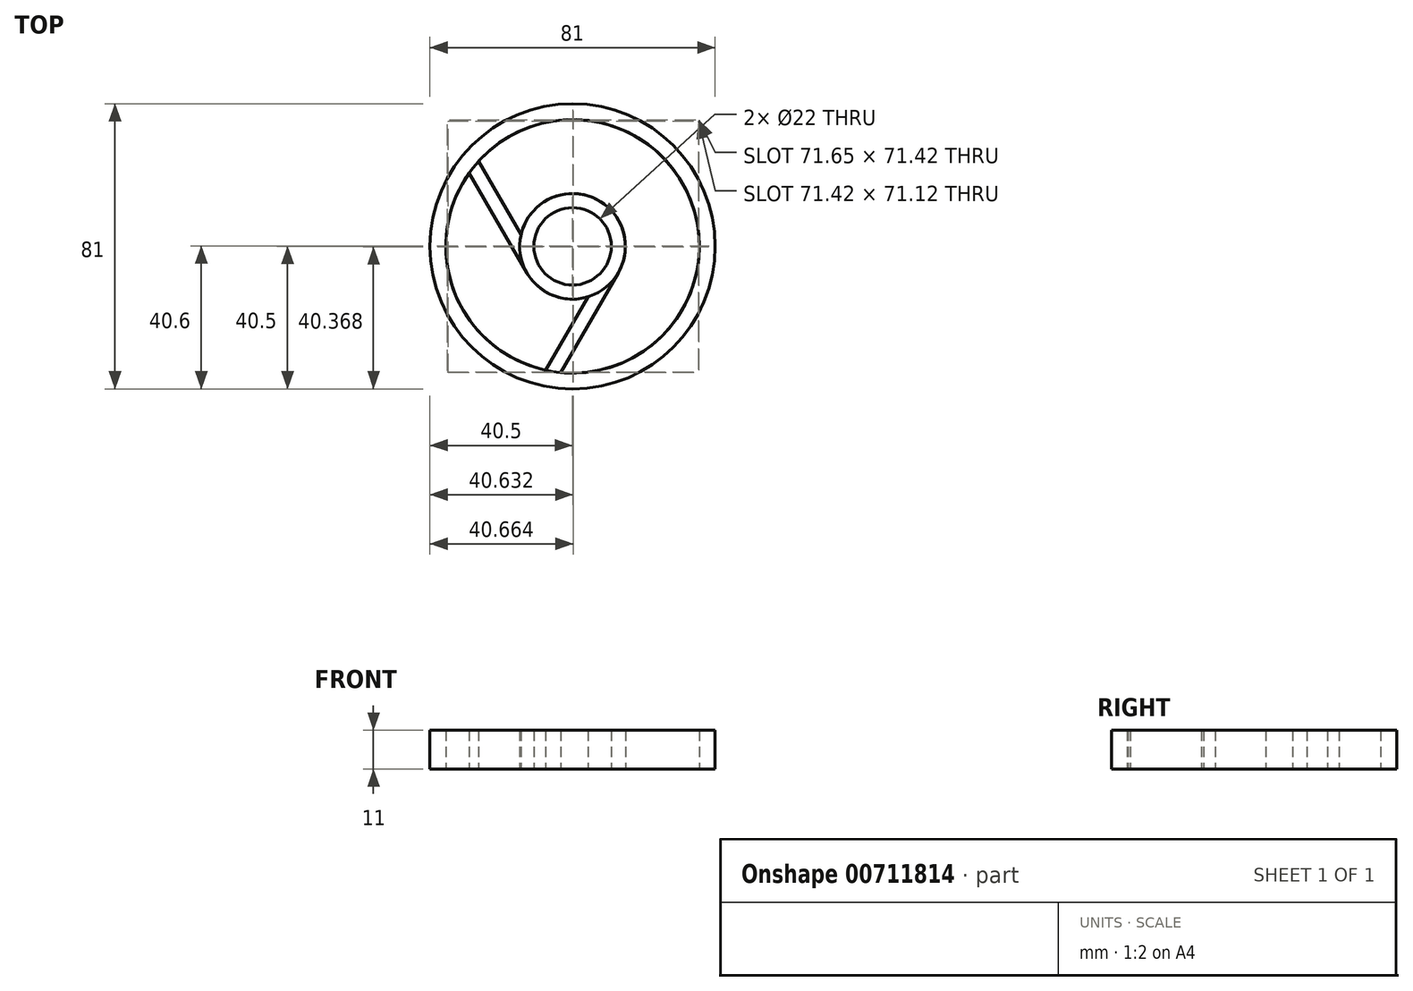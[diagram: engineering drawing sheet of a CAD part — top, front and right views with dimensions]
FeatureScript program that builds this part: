
annotation { "Feature Type Name" : "Feature", "Feature Type Description" : "" }
export const myFeature = defineFeature(function(context is Context, id is Id, definition is map)
    precondition{}
    {
        {
            var Q0;
            Q0=qCreatedBy(makeId("Top.planeOp"),FACE);
            var sketch = newSketch(context, id + "F0", { "sketchPlane" : qUnion([Q0])});
            skCircle(sketch, "E0", {"center": v(0, 0) * mm, "radius": 40.5 * mm});
            skCircle(sketch, "E1", {"center": v(0, 0) * mm, "radius": 36 * mm});
            skCircle(sketch, "E2", {"center": v(0, 0) * mm, "radius": 11 * mm});
            skCircle(sketch, "E3", {"center": v(0, 0) * mm, "radius": 15 * mm});
            skLineSegment(sketch, "E4", {"start": v(0, 15) * mm, "end": v(37.62, 15) * mm});
            skLineSegment(sketch, "E5", {"start": v(0, 11) * mm, "end": v(38.98, 11) * mm});
            skSolve(sketch);
        }
        {
            var Q0;
            {var subQ0=sQuery(id+"F0.wireOp",EDGE,"E4");var subQ1=sQuery(id+"F0.wireOp",EDGE,"E0");var subQ2=makeQuery(id+"F0.imprint","INTERSECT",VERTEX,{"derivedFrom":[subQ1,subQ0]});Q0=makeQuery(id+"F0.imprint","IMPRINT",FACE,{"disambiguationData":[TD([[makeQuery(id+"F0.imprint","IMPRINT",EDGE,{"disambiguationData":[TD([[subQ2,-1.0]])],"derivedFrom":subQ1}),1.0]])]});}
            var Q1;
            Q1=makeQuery(id+"F0.imprint","IMPRINT",FACE,{"disambiguationData":[TD([[makeQuery(id+"F0.imprint","IMPRINT",EDGE,{"derivedFrom":sQuery(id+"F0.wireOp",EDGE,"E2")}),-1.0]])]});
            var Q2;
            {var subQ0=sQuery(id+"F0.wireOp",EDGE,"E4");var subQ1=sQuery(id+"F0.wireOp",EDGE,"E1");var subQ2=makeQuery(id+"F0.imprint","INTERSECT",VERTEX,{"derivedFrom":[subQ1,subQ0]});Q2=makeQuery(id+"F0.imprint","IMPRINT",FACE,{"disambiguationData":[TD([[makeQuery(id+"F0.imprint","IMPRINT",EDGE,{"disambiguationData":[TD([[subQ2,1.0]])],"derivedFrom":subQ1}),1.0]])]});}
            var Q3;
            {var subQ0=sQuery(id+"F0.wireOp",EDGE,"E4");var subQ1=sQuery(id+"F0.wireOp",EDGE,"E0");var subQ2=makeQuery(id+"F0.imprint","INTERSECT",VERTEX,{"derivedFrom":[subQ1,subQ0]});Q3=makeQuery(id+"F0.imprint","IMPRINT",FACE,{"disambiguationData":[TD([[makeQuery(id+"F0.imprint","IMPRINT",EDGE,{"disambiguationData":[TD([[subQ2,1.0]])],"derivedFrom":subQ1}),1.0]])]});}
            extrude(context, id + "F1", {"entities" : qUnion([Q0, Q1, Q2, Q3]), "endBound" : BoundingType.SYMMETRIC, "depth" : 11 * mm, "offsetDistance" : 25 * mm});
        }
        {
            var Q0;
            Q0=makeQuery(id+"F1.opExtrude","SWEPT_BODY",BODY,{"disambiguationData":[OSD([sQuery(id+"F0.wireOp",EDGE,"E0"),sQuery(id+"F0.wireOp",EDGE,"E1"),sQuery(id+"F0.wireOp",EDGE,"E2"),sQuery(id+"F0.wireOp",EDGE,"E3"),sQuery(id+"F0.wireOp",EDGE,"E4"),sQuery(id+"F0.wireOp",EDGE,"E5")])]});
            var Q1;
            Q1=makeQuery(id+"F1.opExtrude","CAP_EDGE",EDGE,{"disambiguationData":[OSD([sQuery(id+"F0.wireOp",EDGE,"E2")])],"isStart":false});
            transform(context, id + "F2", {"entities" : qUnion([Q0]), "transformType" : TransformType.ROTATION, "transformAxis" : qUnion([Q1]), "angle" : 120 * degree, "makeCopy" : true});
        }
        {
            var Q0;
            Q0=makeQuery(id+"F1.opExtrude","SWEPT_BODY",BODY,{"disambiguationData":[OSD([sQuery(id+"F0.wireOp",EDGE,"E0"),sQuery(id+"F0.wireOp",EDGE,"E1"),sQuery(id+"F0.wireOp",EDGE,"E2"),sQuery(id+"F0.wireOp",EDGE,"E3"),sQuery(id+"F0.wireOp",EDGE,"E4"),sQuery(id+"F0.wireOp",EDGE,"E5")])]});
            var Q1;
            Q1=makeQuery(id+"F1.opExtrude","CAP_EDGE",EDGE,{"disambiguationData":[OSD([sQuery(id+"F0.wireOp",EDGE,"E2")])],"isStart":false});
            transform(context, id + "F3", {"entities" : qUnion([Q0]), "transformType" : TransformType.ROTATION, "transformAxis" : qUnion([Q1]), "angle" : 240 * degree, "makeCopy" : true});
        }
        {
            var Q0;
            Q0=qCreatedBy(makeId("Top.planeOp"),FACE);
            var sketch = newSketch(context, id + "F4", { "sketchPlane" : qUnion([Q0])});
            skLineSegment(sketch, "E6", {"start": v(-5.67, 15.8) * mm, "end": v(5.3, 15.8) * mm});
            skLineSegment(sketch, "E7", {"start": v(5.3, 15.8) * mm, "end": v(10.78, 25.3) * mm});
            skLineSegment(sketch, "E8", {"start": v(10.78, 25.3) * mm, "end": v(5.3, 34.8) * mm});
            skLineSegment(sketch, "E9", {"start": v(5.3, 34.8) * mm, "end": v(-5.67, 34.8) * mm});
            skLineSegment(sketch, "E10", {"start": v(-5.67, 34.8) * mm, "end": v(-11.16, 25.3) * mm});
            skLineSegment(sketch, "E11", {"start": v(-11.16, 25.3) * mm, "end": v(-5.67, 15.8) * mm});
            skLineSegment(sketch, "E12", {"start": v(5.3, 34.8) * mm, "end": v(5.3, 15.8) * mm, "construction": true});
            skLineSegment(sketch, "E13", {"start": v(-5.67, 34.8) * mm, "end": v(10.78, 25.3) * mm, "construction": true});
            skLineSegment(sketch, "E14", {"start": v(-11.16, 25.3) * mm, "end": v(5.3, 34.8) * mm, "construction": true});
            skLineSegment(sketch, "E15", {"start": v(0, 0) * mm, "end": v(0, 15.8) * mm, "construction": true});
            skSolve(sketch);
        }
        {
            var Q0;
            Q0=qSketchRegion(id+"F4",true);
            extrude(context, id + "F5", {"entities" : qUnion([Q0]), "operationType" : NewBodyOperationType.REMOVE, "endBound" : BoundingType.SYMMETRIC, "depth" : 11 * mm, "offsetDistance" : 25 * mm});
        }
        {
            var Q0;
            Q0=qCreatedBy(makeId("Top.planeOp"),FACE);
            var sketch = newSketch(context, id + "F6", { "sketchPlane" : qUnion([Q0])});
            skCircle(sketch, "E16", {"center": v(0, 0) * mm, "radius": 36 * mm});
            skCircle(sketch, "E17", {"center": v(0, 0) * mm, "radius": 15 * mm});
            skSolve(sketch);
        }
        {
            var Q0;
            Q0 = qSketchRegion(id + "F6", true);
            extrude(context, id + "F7", {"entities" : qUnion([Q0]), "endBound" : BoundingType.SYMMETRIC, "depth" : 11 * mm, "offsetDistance" : 25 * mm});
        }
        {
            var Q0;
            Q0=makeQuery(id+"F1.opExtrude","SWEPT_BODY",BODY,{"disambiguationData":[OSD([sQuery(id+"F0.wireOp",EDGE,"E0"),sQuery(id+"F0.wireOp",EDGE,"E1"),sQuery(id+"F0.wireOp",EDGE,"E2"),sQuery(id+"F0.wireOp",EDGE,"E3"),sQuery(id+"F0.wireOp",EDGE,"E4"),sQuery(id+"F0.wireOp",EDGE,"E5")])]});
            var Q1;
            Q1=makeQuery(id+"F7.opExtrude","SWEPT_BODY",BODY,{"disambiguationData":[OSD([sQuery(id+"F6.wireOp",EDGE,"E16"),sQuery(id+"F6.wireOp",EDGE,"E17")])]});
            booleanBodies(context, id + "F8", {"operationType" : BooleanOperationType.SUBTRACTION, "tools" : qUnion([Q0]), "targets" : qUnion([Q1])});
        }
        {
            var Q0;
            Q0=makeQuery(id+"F8.opBoolean","SPLIT",BODY,{"disambiguationData":[OD(1.0)],"derivedFrom":makeQuery(id+"F7.opExtrude","SWEPT_BODY",BODY,{"disambiguationData":[OSD([sQuery(id+"F6.wireOp",EDGE,"E16"),sQuery(id+"F6.wireOp",EDGE,"E17")])]})});
            var Q1;
            Q1=makeQuery(id+"F8.opBoolean","SPLIT",BODY,{"disambiguationData":[OD(2.0)],"derivedFrom":makeQuery(id+"F7.opExtrude","SWEPT_BODY",BODY,{"disambiguationData":[OSD([sQuery(id+"F6.wireOp",EDGE,"E16"),sQuery(id+"F6.wireOp",EDGE,"E17")])]})});
            deleteBodies(context, id + "F9", {"entities" : qUnion([Q0, Q1])});
        }
        {
            var Q0;
            Q0=qCreatedBy(makeId("Top.planeOp"),FACE);
            var sketch = newSketch(context, id + "F10", { "sketchPlane" : qUnion([Q0])});
            skCircle(sketch, "E18.cCircle", {"center": v(0, 25.3) * mm, "radius": 9.5 * mm, "construction": true});
            skLineSegment(sketch, "E18.0", {"start": v(10.97, 25.3) * mm, "end": v(5.48, 15.8) * mm});
            skLineSegment(sketch, "E18.1", {"start": v(5.48, 15.8) * mm, "end": v(-5.48, 15.8) * mm});
            skLineSegment(sketch, "E18.2", {"start": v(-5.48, 15.8) * mm, "end": v(-10.97, 25.3) * mm});
            skLineSegment(sketch, "E18.3", {"start": v(-10.97, 25.3) * mm, "end": v(-5.48, 34.8) * mm});
            skLineSegment(sketch, "E18.4", {"start": v(-5.48, 34.8) * mm, "end": v(5.48, 34.8) * mm});
            skLineSegment(sketch, "E18.5", {"start": v(5.48, 34.8) * mm, "end": v(10.97, 25.3) * mm});
            skPoint(sketch, "E18.0.midPoint", {"position": v(8.23, 20.55) * mm});
            skLineSegment(sketch, "E19", {"start": v(-5.48, 15.8) * mm, "end": v(-5.48, 34.8) * mm, "construction": true});
            skLineSegment(sketch, "E20", {"start": v(0, 0) * mm, "end": v(0, 15.8) * mm, "construction": true});
            skSolve(sketch);
        }
        {
            var Q0;
            Q0 = qSketchRegion(id + "F10", true);
            extrude(context, id + "F11", {"entities" : qUnion([Q0]), "operationType" : NewBodyOperationType.REMOVE, "endBound" : BoundingType.SYMMETRIC, "depth" : 11 * mm, "offsetDistance" : 25 * mm});
        }
    });
